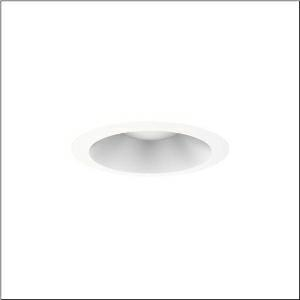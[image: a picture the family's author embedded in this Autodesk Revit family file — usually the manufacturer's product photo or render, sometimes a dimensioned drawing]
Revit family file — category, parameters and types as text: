
# Revit family: lunis_31-l_51dn16eg32b
name_source: partatom
category: Lighting Fixtures
units: mm (PartAtom-declared; Revit-internal decimal feet)

## family parameters
Cut with Voids When Loaded = No
Host = Face
Light Source = No
Part Type = Normal
Room Calculation Point = No
Round Connector Dimension = Use Diameter
Shared = No

## types (1)
- --- (1 x LED, 2500 lm, 17 W, 3000K)
    Apparent Load = 17 VA
    CIE Flux Codes = 64 93 99 100 100
    Color Rendering = 80
    Color Temperature = 3000K
    Default Elevation = 1800 mm
    Description = Lunis 31, -L, downlight, light control with reflector, light emission: direct distribution, LED rated luminous flux: 2.500lm, light colour: 830, mains connection: 220..240V, AC, 50/60Hz, housing, of aluminium, white, protection rating (complete): IP20, protection rating (on room side): IP54, insulation class (complete): insulation class II (safety insulation), certification: CE, packaging unit: 1 piece
    Height = 0 mm  [stored 0 ft]
    Lamp = 1 x LED
    Lamp Light Flux = 2500 lm
    Lamp Power = 17 W
    Lamp count = 1
    Length = 259 mm
    Luminous efficacy = 147 lm/W
    Manufacturer = Siteco
    ModVariant = No
    Model = 51DN16EG32B
    Mounting Place = Ceiling
    Mounting Type = Recessed
    Number of Poles = 1
    OnlyDefault = Yes
    Power Factor = 1
    Product Name = Lunis 31-L
    Product group = downlight
    ProductGroupID = 400
    Protection Class = Protection class II
    Protection Degree = IP 20
    RLX_Detail_Level = 1
    RLX_Emergency_Light_Flux = 0 lm
    RLX_Emergency_Type = 0
    RLX_Emergency_Type_DB = No
    RlxData = <blob elided: 24261 chars, md5=91133cb1>
    Socket = socket
    Standby Power = 0 W
    System Light Flux = 2500 lm
    System Power = 17 W
    Type Comments = individual setting: luminous flux: 100 % | (ON | OFF | ON) | 450 mA
    Type Image = l_1345915.jpg
    URL = http://relux.com
    VarID = @adj_010103
    Voltage = 0 V
    Weight = 0.00 kg
    Width = 0 mm  [stored 0 ft]

note: [stored X ft] marks values corroborated as IEEE doubles in the binary element streams (Revit-internal decimal feet)

## geometry (parser evidence)
native form markers: Blend x4, Sweep x12
no freeform markers — native parametric forms only
